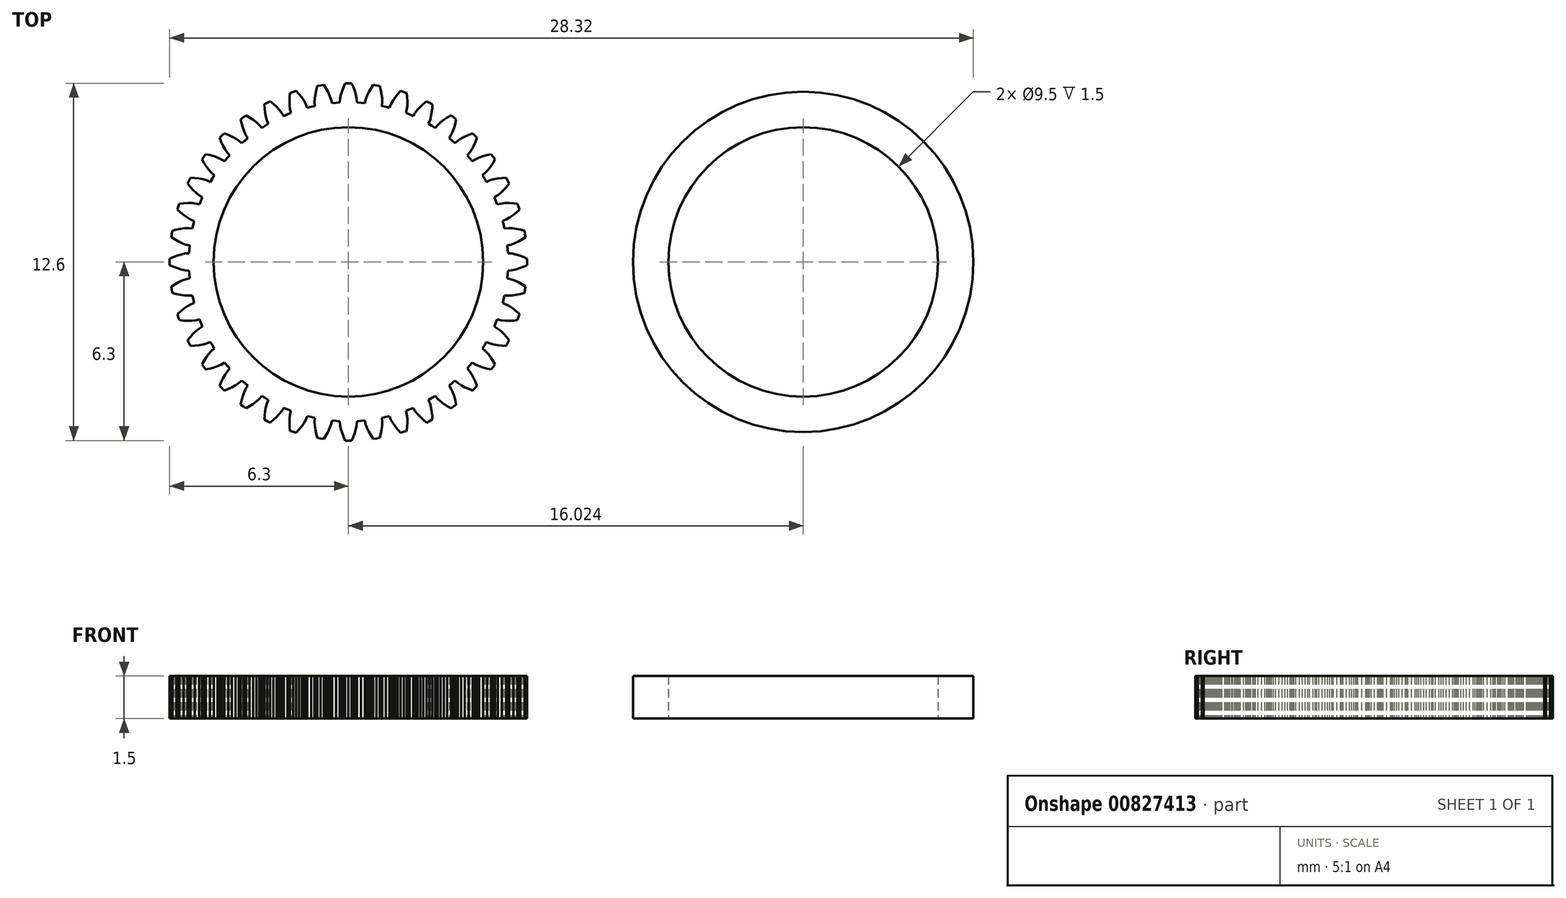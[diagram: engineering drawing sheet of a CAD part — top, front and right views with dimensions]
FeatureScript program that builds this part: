
annotation { "Feature Type Name" : "Feature", "Feature Type Description" : "" }
export const myFeature = defineFeature(function(context is Context, id is Id, definition is map)
    precondition{}
    {
        {
            var Q0;
            Q0=qCreatedBy(makeId("Top.planeOp"),FACE);
            var sketch = newSketch(context, id + "F0", { "sketchPlane" : qUnion([Q0])});
            skLineSegment(sketch, "E0", {"start": v(5.6, -0.44) * mm, "end": v(5.62, -0.3) * mm});
            skLineSegment(sketch, "E1", {"start": v(5.62, -0.3) * mm, "end": v(5.75, -0.3) * mm});
            skLineSegment(sketch, "E2", {"start": v(5.75, -0.3) * mm, "end": v(5.89, -0.27) * mm});
            skLineSegment(sketch, "E3", {"start": v(5.89, -0.27) * mm, "end": v(6.03, -0.23) * mm});
            skLineSegment(sketch, "E4", {"start": v(6.03, -0.23) * mm, "end": v(6.16, -0.17) * mm});
            skLineSegment(sketch, "E5", {"start": v(6.16, -0.17) * mm, "end": v(6.3, -0.11) * mm});
            skLineSegment(sketch, "E6", {"start": v(6.3, -0.11) * mm, "end": v(6.3, 0) * mm});
            skLineSegment(sketch, "E7", {"start": v(6.3, 0) * mm, "end": v(6.3, 0.11) * mm});
            skLineSegment(sketch, "E8", {"start": v(6.3, 0.11) * mm, "end": v(6.16, 0.17) * mm});
            skLineSegment(sketch, "E9", {"start": v(6.16, 0.17) * mm, "end": v(6.03, 0.23) * mm});
            skLineSegment(sketch, "E10", {"start": v(6.03, 0.23) * mm, "end": v(5.89, 0.27) * mm});
            skLineSegment(sketch, "E11", {"start": v(5.89, 0.27) * mm, "end": v(5.75, 0.3) * mm});
            skLineSegment(sketch, "E12", {"start": v(5.75, 0.3) * mm, "end": v(5.62, 0.3) * mm});
            skLineSegment(sketch, "E13", {"start": v(5.62, 0.3) * mm, "end": v(5.6, 0.44) * mm});
            skLineSegment(sketch, "E14", {"start": v(5.6, 0.44) * mm, "end": v(5.6, 0.58) * mm});
            skLineSegment(sketch, "E15", {"start": v(5.6, 0.58) * mm, "end": v(5.73, 0.6) * mm});
            skLineSegment(sketch, "E16", {"start": v(5.73, 0.6) * mm, "end": v(5.86, 0.66) * mm});
            skLineSegment(sketch, "E17", {"start": v(5.86, 0.66) * mm, "end": v(5.99, 0.72) * mm});
            skLineSegment(sketch, "E18", {"start": v(5.99, 0.72) * mm, "end": v(6.11, 0.8) * mm});
            skLineSegment(sketch, "E19", {"start": v(6.11, 0.8) * mm, "end": v(6.24, 0.87) * mm});
            skLineSegment(sketch, "E20", {"start": v(6.24, 0.87) * mm, "end": v(6.22, 0.99) * mm});
            skLineSegment(sketch, "E21", {"start": v(6.22, 0.99) * mm, "end": v(6.2, 1.1) * mm});
            skLineSegment(sketch, "E22", {"start": v(6.2, 1.1) * mm, "end": v(6.06, 1.14) * mm});
            skLineSegment(sketch, "E23", {"start": v(6.06, 1.14) * mm, "end": v(5.92, 1.17) * mm});
            skLineSegment(sketch, "E24", {"start": v(5.92, 1.17) * mm, "end": v(5.77, 1.18) * mm});
            skLineSegment(sketch, "E25", {"start": v(5.77, 1.18) * mm, "end": v(5.64, 1.2) * mm});
            skLineSegment(sketch, "E26", {"start": v(5.64, 1.2) * mm, "end": v(5.5, 1.18) * mm});
            skLineSegment(sketch, "E27", {"start": v(5.5, 1.18) * mm, "end": v(5.47, 1.31) * mm});
            skLineSegment(sketch, "E28", {"start": v(5.47, 1.31) * mm, "end": v(5.44, 1.45) * mm});
            skLineSegment(sketch, "E29", {"start": v(5.44, 1.45) * mm, "end": v(5.56, 1.5) * mm});
            skLineSegment(sketch, "E30", {"start": v(5.56, 1.5) * mm, "end": v(5.68, 1.57) * mm});
            skLineSegment(sketch, "E31", {"start": v(5.68, 1.57) * mm, "end": v(5.8, 1.65) * mm});
            skLineSegment(sketch, "E32", {"start": v(5.8, 1.65) * mm, "end": v(5.91, 1.74) * mm});
            skLineSegment(sketch, "E33", {"start": v(5.91, 1.74) * mm, "end": v(6.03, 1.84) * mm});
            skLineSegment(sketch, "E34", {"start": v(6.03, 1.84) * mm, "end": v(6, 1.95) * mm});
            skLineSegment(sketch, "E35", {"start": v(6, 1.95) * mm, "end": v(5.96, 2.05) * mm});
            skLineSegment(sketch, "E36", {"start": v(5.96, 2.05) * mm, "end": v(5.8, 2.07) * mm});
            skLineSegment(sketch, "E37", {"start": v(5.8, 2.07) * mm, "end": v(5.66, 2.08) * mm});
            skLineSegment(sketch, "E38", {"start": v(5.66, 2.08) * mm, "end": v(5.52, 2.07) * mm});
            skLineSegment(sketch, "E39", {"start": v(5.52, 2.07) * mm, "end": v(5.38, 2.06) * mm});
            skLineSegment(sketch, "E40", {"start": v(5.38, 2.06) * mm, "end": v(5.25, 2.03) * mm});
            skLineSegment(sketch, "E41", {"start": v(5.25, 2.03) * mm, "end": v(5.2, 2.15) * mm});
            skLineSegment(sketch, "E42", {"start": v(5.2, 2.15) * mm, "end": v(5.14, 2.28) * mm});
            skLineSegment(sketch, "E43", {"start": v(5.14, 2.28) * mm, "end": v(5.26, 2.35) * mm});
            skLineSegment(sketch, "E44", {"start": v(5.26, 2.35) * mm, "end": v(5.37, 2.44) * mm});
            skLineSegment(sketch, "E45", {"start": v(5.37, 2.44) * mm, "end": v(5.47, 2.53) * mm});
            skLineSegment(sketch, "E46", {"start": v(5.47, 2.53) * mm, "end": v(5.57, 2.64) * mm});
            skLineSegment(sketch, "E47", {"start": v(5.57, 2.64) * mm, "end": v(5.66, 2.76) * mm});
            skLineSegment(sketch, "E48", {"start": v(5.66, 2.76) * mm, "end": v(5.61, 2.86) * mm});
            skLineSegment(sketch, "E49", {"start": v(5.61, 2.86) * mm, "end": v(5.56, 2.96) * mm});
            skLineSegment(sketch, "E50", {"start": v(5.56, 2.96) * mm, "end": v(5.41, 2.95) * mm});
            skLineSegment(sketch, "E51", {"start": v(5.41, 2.95) * mm, "end": v(5.27, 2.94) * mm});
            skLineSegment(sketch, "E52", {"start": v(5.27, 2.94) * mm, "end": v(5.13, 2.91) * mm});
            skLineSegment(sketch, "E53", {"start": v(5.13, 2.91) * mm, "end": v(5, 2.87) * mm});
            skLineSegment(sketch, "E54", {"start": v(5, 2.87) * mm, "end": v(4.87, 2.82) * mm});
            skLineSegment(sketch, "E55", {"start": v(4.87, 2.82) * mm, "end": v(4.8, 2.94) * mm});
            skLineSegment(sketch, "E56", {"start": v(4.8, 2.94) * mm, "end": v(4.72, 3.06) * mm});
            skLineSegment(sketch, "E57", {"start": v(4.72, 3.06) * mm, "end": v(4.83, 3.14) * mm});
            skLineSegment(sketch, "E58", {"start": v(4.83, 3.14) * mm, "end": v(4.92, 3.25) * mm});
            skLineSegment(sketch, "E59", {"start": v(4.92, 3.25) * mm, "end": v(5, 3.36) * mm});
            skLineSegment(sketch, "E60", {"start": v(5, 3.36) * mm, "end": v(5.09, 3.48) * mm});
            skLineSegment(sketch, "E61", {"start": v(5.09, 3.48) * mm, "end": v(5.16, 3.61) * mm});
            skLineSegment(sketch, "E62", {"start": v(5.16, 3.61) * mm, "end": v(5.1, 3.7) * mm});
            skLineSegment(sketch, "E63", {"start": v(5.1, 3.7) * mm, "end": v(5.03, 3.8) * mm});
            skLineSegment(sketch, "E64", {"start": v(5.03, 3.8) * mm, "end": v(4.88, 3.76) * mm});
            skLineSegment(sketch, "E65", {"start": v(4.88, 3.76) * mm, "end": v(4.74, 3.72) * mm});
            skLineSegment(sketch, "E66", {"start": v(4.74, 3.72) * mm, "end": v(4.6, 3.68) * mm});
            skLineSegment(sketch, "E67", {"start": v(4.6, 3.68) * mm, "end": v(4.48, 3.62) * mm});
            skLineSegment(sketch, "E68", {"start": v(4.48, 3.62) * mm, "end": v(4.37, 3.55) * mm});
            skLineSegment(sketch, "E69", {"start": v(4.37, 3.55) * mm, "end": v(4.28, 3.65) * mm});
            skLineSegment(sketch, "E70", {"start": v(4.28, 3.65) * mm, "end": v(4.19, 3.76) * mm});
            skLineSegment(sketch, "E71", {"start": v(4.19, 3.76) * mm, "end": v(4.28, 3.86) * mm});
            skLineSegment(sketch, "E72", {"start": v(4.28, 3.86) * mm, "end": v(4.35, 3.98) * mm});
            skLineSegment(sketch, "E73", {"start": v(4.35, 3.98) * mm, "end": v(4.42, 4.1) * mm});
            skLineSegment(sketch, "E74", {"start": v(4.42, 4.1) * mm, "end": v(4.48, 4.23) * mm});
            skLineSegment(sketch, "E75", {"start": v(4.48, 4.23) * mm, "end": v(4.53, 4.37) * mm});
            skLineSegment(sketch, "E76", {"start": v(4.53, 4.37) * mm, "end": v(4.45, 4.45) * mm});
            skLineSegment(sketch, "E77", {"start": v(4.45, 4.45) * mm, "end": v(4.37, 4.53) * mm});
            skLineSegment(sketch, "E78", {"start": v(4.37, 4.53) * mm, "end": v(4.23, 4.48) * mm});
            skLineSegment(sketch, "E79", {"start": v(4.23, 4.48) * mm, "end": v(4.1, 4.42) * mm});
            skLineSegment(sketch, "E80", {"start": v(4.1, 4.42) * mm, "end": v(3.98, 4.35) * mm});
            skLineSegment(sketch, "E81", {"start": v(3.98, 4.35) * mm, "end": v(3.86, 4.28) * mm});
            skLineSegment(sketch, "E82", {"start": v(3.86, 4.28) * mm, "end": v(3.76, 4.19) * mm});
            skLineSegment(sketch, "E83", {"start": v(3.76, 4.19) * mm, "end": v(3.65, 4.28) * mm});
            skLineSegment(sketch, "E84", {"start": v(3.65, 4.28) * mm, "end": v(3.55, 4.37) * mm});
            skLineSegment(sketch, "E85", {"start": v(3.55, 4.37) * mm, "end": v(3.62, 4.48) * mm});
            skLineSegment(sketch, "E86", {"start": v(3.62, 4.48) * mm, "end": v(3.68, 4.6) * mm});
            skLineSegment(sketch, "E87", {"start": v(3.68, 4.6) * mm, "end": v(3.72, 4.74) * mm});
            skLineSegment(sketch, "E88", {"start": v(3.72, 4.74) * mm, "end": v(3.76, 4.88) * mm});
            skLineSegment(sketch, "E89", {"start": v(3.76, 4.88) * mm, "end": v(3.8, 5.03) * mm});
            skLineSegment(sketch, "E90", {"start": v(3.8, 5.03) * mm, "end": v(3.7, 5.1) * mm});
            skLineSegment(sketch, "E91", {"start": v(3.7, 5.1) * mm, "end": v(3.61, 5.16) * mm});
            skLineSegment(sketch, "E92", {"start": v(3.61, 5.16) * mm, "end": v(3.48, 5.09) * mm});
            skLineSegment(sketch, "E93", {"start": v(3.48, 5.09) * mm, "end": v(3.36, 5) * mm});
            skLineSegment(sketch, "E94", {"start": v(3.36, 5) * mm, "end": v(3.25, 4.92) * mm});
            skLineSegment(sketch, "E95", {"start": v(3.25, 4.92) * mm, "end": v(3.14, 4.83) * mm});
            skLineSegment(sketch, "E96", {"start": v(3.14, 4.83) * mm, "end": v(3.06, 4.72) * mm});
            skLineSegment(sketch, "E97", {"start": v(3.06, 4.72) * mm, "end": v(2.94, 4.8) * mm});
            skLineSegment(sketch, "E98", {"start": v(2.94, 4.8) * mm, "end": v(2.82, 4.87) * mm});
            skLineSegment(sketch, "E99", {"start": v(2.82, 4.87) * mm, "end": v(2.87, 5) * mm});
            skLineSegment(sketch, "E100", {"start": v(2.87, 5) * mm, "end": v(2.91, 5.13) * mm});
            skLineSegment(sketch, "E101", {"start": v(2.91, 5.13) * mm, "end": v(2.94, 5.27) * mm});
            skLineSegment(sketch, "E102", {"start": v(2.94, 5.27) * mm, "end": v(2.95, 5.41) * mm});
            skLineSegment(sketch, "E103", {"start": v(2.95, 5.41) * mm, "end": v(2.96, 5.56) * mm});
            skLineSegment(sketch, "E104", {"start": v(2.96, 5.56) * mm, "end": v(2.86, 5.61) * mm});
            skLineSegment(sketch, "E105", {"start": v(2.86, 5.61) * mm, "end": v(2.76, 5.66) * mm});
            skLineSegment(sketch, "E106", {"start": v(2.76, 5.66) * mm, "end": v(2.64, 5.57) * mm});
            skLineSegment(sketch, "E107", {"start": v(2.64, 5.57) * mm, "end": v(2.53, 5.47) * mm});
            skLineSegment(sketch, "E108", {"start": v(2.53, 5.47) * mm, "end": v(2.44, 5.37) * mm});
            skLineSegment(sketch, "E109", {"start": v(2.44, 5.37) * mm, "end": v(2.35, 5.26) * mm});
            skLineSegment(sketch, "E110", {"start": v(2.35, 5.26) * mm, "end": v(2.28, 5.14) * mm});
            skLineSegment(sketch, "E111", {"start": v(2.28, 5.14) * mm, "end": v(2.15, 5.2) * mm});
            skLineSegment(sketch, "E112", {"start": v(2.15, 5.2) * mm, "end": v(2.03, 5.25) * mm});
            skLineSegment(sketch, "E113", {"start": v(2.03, 5.25) * mm, "end": v(2.06, 5.38) * mm});
            skLineSegment(sketch, "E114", {"start": v(2.06, 5.38) * mm, "end": v(2.07, 5.52) * mm});
            skLineSegment(sketch, "E115", {"start": v(2.07, 5.52) * mm, "end": v(2.08, 5.66) * mm});
            skLineSegment(sketch, "E116", {"start": v(2.08, 5.66) * mm, "end": v(2.07, 5.8) * mm});
            skLineSegment(sketch, "E117", {"start": v(2.07, 5.8) * mm, "end": v(2.05, 5.96) * mm});
            skLineSegment(sketch, "E118", {"start": v(2.05, 5.96) * mm, "end": v(1.95, 6) * mm});
            skLineSegment(sketch, "E119", {"start": v(1.95, 6) * mm, "end": v(1.84, 6.03) * mm});
            skLineSegment(sketch, "E120", {"start": v(1.84, 6.03) * mm, "end": v(1.74, 5.91) * mm});
            skLineSegment(sketch, "E121", {"start": v(1.74, 5.91) * mm, "end": v(1.65, 5.8) * mm});
            skLineSegment(sketch, "E122", {"start": v(1.65, 5.8) * mm, "end": v(1.57, 5.68) * mm});
            skLineSegment(sketch, "E123", {"start": v(1.57, 5.68) * mm, "end": v(1.5, 5.56) * mm});
            skLineSegment(sketch, "E124", {"start": v(1.5, 5.56) * mm, "end": v(1.45, 5.44) * mm});
            skLineSegment(sketch, "E125", {"start": v(1.45, 5.44) * mm, "end": v(1.31, 5.47) * mm});
            skLineSegment(sketch, "E126", {"start": v(1.31, 5.47) * mm, "end": v(1.18, 5.5) * mm});
            skLineSegment(sketch, "E127", {"start": v(1.18, 5.5) * mm, "end": v(1.2, 5.64) * mm});
            skLineSegment(sketch, "E128", {"start": v(1.2, 5.64) * mm, "end": v(1.18, 5.77) * mm});
            skLineSegment(sketch, "E129", {"start": v(1.18, 5.77) * mm, "end": v(1.17, 5.92) * mm});
            skLineSegment(sketch, "E130", {"start": v(1.17, 5.92) * mm, "end": v(1.14, 6.06) * mm});
            skLineSegment(sketch, "E131", {"start": v(1.14, 6.06) * mm, "end": v(1.1, 6.2) * mm});
            skLineSegment(sketch, "E132", {"start": v(1.1, 6.2) * mm, "end": v(0.99, 6.22) * mm});
            skLineSegment(sketch, "E133", {"start": v(0.99, 6.22) * mm, "end": v(0.87, 6.24) * mm});
            skLineSegment(sketch, "E134", {"start": v(0.87, 6.24) * mm, "end": v(0.8, 6.11) * mm});
            skLineSegment(sketch, "E135", {"start": v(0.8, 6.11) * mm, "end": v(0.72, 5.99) * mm});
            skLineSegment(sketch, "E136", {"start": v(0.72, 5.99) * mm, "end": v(0.66, 5.86) * mm});
            skLineSegment(sketch, "E137", {"start": v(0.66, 5.86) * mm, "end": v(0.6, 5.73) * mm});
            skLineSegment(sketch, "E138", {"start": v(0.6, 5.73) * mm, "end": v(0.58, 5.6) * mm});
            skLineSegment(sketch, "E139", {"start": v(0.58, 5.6) * mm, "end": v(0.44, 5.6) * mm});
            skLineSegment(sketch, "E140", {"start": v(0.44, 5.6) * mm, "end": v(0.3, 5.62) * mm});
            skLineSegment(sketch, "E141", {"start": v(0.3, 5.62) * mm, "end": v(0.3, 5.75) * mm});
            skLineSegment(sketch, "E142", {"start": v(0.3, 5.75) * mm, "end": v(0.27, 5.89) * mm});
            skLineSegment(sketch, "E143", {"start": v(0.27, 5.89) * mm, "end": v(0.23, 6.03) * mm});
            skLineSegment(sketch, "E144", {"start": v(0.23, 6.03) * mm, "end": v(0.17, 6.16) * mm});
            skLineSegment(sketch, "E145", {"start": v(0.17, 6.16) * mm, "end": v(0.11, 6.3) * mm});
            skLineSegment(sketch, "E146", {"start": v(0.11, 6.3) * mm, "end": v(0, 6.3) * mm});
            skLineSegment(sketch, "E147", {"start": v(0, 6.3) * mm, "end": v(-0.11, 6.3) * mm});
            skLineSegment(sketch, "E148", {"start": v(-0.11, 6.3) * mm, "end": v(-0.17, 6.16) * mm});
            skLineSegment(sketch, "E149", {"start": v(-0.17, 6.16) * mm, "end": v(-0.23, 6.03) * mm});
            skLineSegment(sketch, "E150", {"start": v(-0.23, 6.03) * mm, "end": v(-0.27, 5.89) * mm});
            skLineSegment(sketch, "E151", {"start": v(-0.27, 5.89) * mm, "end": v(-0.3, 5.75) * mm});
            skLineSegment(sketch, "E152", {"start": v(-0.3, 5.75) * mm, "end": v(-0.3, 5.62) * mm});
            skLineSegment(sketch, "E153", {"start": v(-0.3, 5.62) * mm, "end": v(-0.44, 5.6) * mm});
            skLineSegment(sketch, "E154", {"start": v(-0.44, 5.6) * mm, "end": v(-0.58, 5.6) * mm});
            skLineSegment(sketch, "E155", {"start": v(-0.58, 5.6) * mm, "end": v(-0.6, 5.73) * mm});
            skLineSegment(sketch, "E156", {"start": v(-0.6, 5.73) * mm, "end": v(-0.66, 5.86) * mm});
            skLineSegment(sketch, "E157", {"start": v(-0.66, 5.86) * mm, "end": v(-0.72, 5.99) * mm});
            skLineSegment(sketch, "E158", {"start": v(-0.72, 5.99) * mm, "end": v(-0.8, 6.11) * mm});
            skLineSegment(sketch, "E159", {"start": v(-0.8, 6.11) * mm, "end": v(-0.87, 6.24) * mm});
            skLineSegment(sketch, "E160", {"start": v(-0.87, 6.24) * mm, "end": v(-0.99, 6.22) * mm});
            skLineSegment(sketch, "E161", {"start": v(-0.99, 6.22) * mm, "end": v(-1.1, 6.2) * mm});
            skLineSegment(sketch, "E162", {"start": v(-1.1, 6.2) * mm, "end": v(-1.14, 6.06) * mm});
            skLineSegment(sketch, "E163", {"start": v(-1.14, 6.06) * mm, "end": v(-1.17, 5.92) * mm});
            skLineSegment(sketch, "E164", {"start": v(-1.17, 5.92) * mm, "end": v(-1.18, 5.77) * mm});
            skLineSegment(sketch, "E165", {"start": v(-1.18, 5.77) * mm, "end": v(-1.2, 5.64) * mm});
            skLineSegment(sketch, "E166", {"start": v(-1.2, 5.64) * mm, "end": v(-1.18, 5.5) * mm});
            skLineSegment(sketch, "E167", {"start": v(-1.18, 5.5) * mm, "end": v(-1.31, 5.47) * mm});
            skLineSegment(sketch, "E168", {"start": v(-1.31, 5.47) * mm, "end": v(-1.45, 5.44) * mm});
            skLineSegment(sketch, "E169", {"start": v(-1.45, 5.44) * mm, "end": v(-1.5, 5.56) * mm});
            skLineSegment(sketch, "E170", {"start": v(-1.5, 5.56) * mm, "end": v(-1.57, 5.68) * mm});
            skLineSegment(sketch, "E171", {"start": v(-1.57, 5.68) * mm, "end": v(-1.65, 5.8) * mm});
            skLineSegment(sketch, "E172", {"start": v(-1.65, 5.8) * mm, "end": v(-1.74, 5.91) * mm});
            skLineSegment(sketch, "E173", {"start": v(-1.74, 5.91) * mm, "end": v(-1.84, 6.03) * mm});
            skLineSegment(sketch, "E174", {"start": v(-1.84, 6.03) * mm, "end": v(-1.95, 6) * mm});
            skLineSegment(sketch, "E175", {"start": v(-1.95, 6) * mm, "end": v(-2.05, 5.96) * mm});
            skLineSegment(sketch, "E176", {"start": v(-2.05, 5.96) * mm, "end": v(-2.07, 5.8) * mm});
            skLineSegment(sketch, "E177", {"start": v(-2.07, 5.8) * mm, "end": v(-2.08, 5.66) * mm});
            skLineSegment(sketch, "E178", {"start": v(-2.08, 5.66) * mm, "end": v(-2.07, 5.52) * mm});
            skLineSegment(sketch, "E179", {"start": v(-2.07, 5.52) * mm, "end": v(-2.06, 5.38) * mm});
            skLineSegment(sketch, "E180", {"start": v(-2.06, 5.38) * mm, "end": v(-2.03, 5.25) * mm});
            skLineSegment(sketch, "E181", {"start": v(-2.03, 5.25) * mm, "end": v(-2.15, 5.2) * mm});
            skLineSegment(sketch, "E182", {"start": v(-2.15, 5.2) * mm, "end": v(-2.28, 5.14) * mm});
            skLineSegment(sketch, "E183", {"start": v(-2.28, 5.14) * mm, "end": v(-2.35, 5.26) * mm});
            skLineSegment(sketch, "E184", {"start": v(-2.35, 5.26) * mm, "end": v(-2.44, 5.37) * mm});
            skLineSegment(sketch, "E185", {"start": v(-2.44, 5.37) * mm, "end": v(-2.53, 5.47) * mm});
            skLineSegment(sketch, "E186", {"start": v(-2.53, 5.47) * mm, "end": v(-2.64, 5.57) * mm});
            skLineSegment(sketch, "E187", {"start": v(-2.64, 5.57) * mm, "end": v(-2.76, 5.66) * mm});
            skLineSegment(sketch, "E188", {"start": v(-2.76, 5.66) * mm, "end": v(-2.86, 5.61) * mm});
            skLineSegment(sketch, "E189", {"start": v(-2.86, 5.61) * mm, "end": v(-2.96, 5.56) * mm});
            skLineSegment(sketch, "E190", {"start": v(-2.96, 5.56) * mm, "end": v(-2.95, 5.41) * mm});
            skLineSegment(sketch, "E191", {"start": v(-2.95, 5.41) * mm, "end": v(-2.94, 5.27) * mm});
            skLineSegment(sketch, "E192", {"start": v(-2.94, 5.27) * mm, "end": v(-2.91, 5.13) * mm});
            skLineSegment(sketch, "E193", {"start": v(-2.91, 5.13) * mm, "end": v(-2.87, 5) * mm});
            skLineSegment(sketch, "E194", {"start": v(-2.87, 5) * mm, "end": v(-2.82, 4.87) * mm});
            skLineSegment(sketch, "E195", {"start": v(-2.82, 4.87) * mm, "end": v(-2.94, 4.8) * mm});
            skLineSegment(sketch, "E196", {"start": v(-2.94, 4.8) * mm, "end": v(-3.06, 4.72) * mm});
            skLineSegment(sketch, "E197", {"start": v(-3.06, 4.72) * mm, "end": v(-3.14, 4.83) * mm});
            skLineSegment(sketch, "E198", {"start": v(-3.14, 4.83) * mm, "end": v(-3.25, 4.92) * mm});
            skLineSegment(sketch, "E199", {"start": v(-3.25, 4.92) * mm, "end": v(-3.36, 5) * mm});
            skLineSegment(sketch, "E200", {"start": v(-3.36, 5) * mm, "end": v(-3.48, 5.09) * mm});
            skLineSegment(sketch, "E201", {"start": v(-3.48, 5.09) * mm, "end": v(-3.61, 5.16) * mm});
            skLineSegment(sketch, "E202", {"start": v(-3.61, 5.16) * mm, "end": v(-3.7, 5.1) * mm});
            skLineSegment(sketch, "E203", {"start": v(-3.7, 5.1) * mm, "end": v(-3.8, 5.03) * mm});
            skLineSegment(sketch, "E204", {"start": v(-3.8, 5.03) * mm, "end": v(-3.76, 4.88) * mm});
            skLineSegment(sketch, "E205", {"start": v(-3.76, 4.88) * mm, "end": v(-3.72, 4.74) * mm});
            skLineSegment(sketch, "E206", {"start": v(-3.72, 4.74) * mm, "end": v(-3.68, 4.6) * mm});
            skLineSegment(sketch, "E207", {"start": v(-3.68, 4.6) * mm, "end": v(-3.62, 4.48) * mm});
            skLineSegment(sketch, "E208", {"start": v(-3.62, 4.48) * mm, "end": v(-3.55, 4.37) * mm});
            skLineSegment(sketch, "E209", {"start": v(-3.55, 4.37) * mm, "end": v(-3.65, 4.28) * mm});
            skLineSegment(sketch, "E210", {"start": v(-3.65, 4.28) * mm, "end": v(-3.76, 4.19) * mm});
            skLineSegment(sketch, "E211", {"start": v(-3.76, 4.19) * mm, "end": v(-3.86, 4.28) * mm});
            skLineSegment(sketch, "E212", {"start": v(-3.86, 4.28) * mm, "end": v(-3.98, 4.35) * mm});
            skLineSegment(sketch, "E213", {"start": v(-3.98, 4.35) * mm, "end": v(-4.1, 4.42) * mm});
            skLineSegment(sketch, "E214", {"start": v(-4.1, 4.42) * mm, "end": v(-4.23, 4.48) * mm});
            skLineSegment(sketch, "E215", {"start": v(-4.23, 4.48) * mm, "end": v(-4.37, 4.53) * mm});
            skLineSegment(sketch, "E216", {"start": v(-4.37, 4.53) * mm, "end": v(-4.45, 4.45) * mm});
            skLineSegment(sketch, "E217", {"start": v(-4.45, 4.45) * mm, "end": v(-4.53, 4.37) * mm});
            skLineSegment(sketch, "E218", {"start": v(-4.53, 4.37) * mm, "end": v(-4.48, 4.23) * mm});
            skLineSegment(sketch, "E219", {"start": v(-4.48, 4.23) * mm, "end": v(-4.42, 4.1) * mm});
            skLineSegment(sketch, "E220", {"start": v(-4.42, 4.1) * mm, "end": v(-4.35, 3.98) * mm});
            skLineSegment(sketch, "E221", {"start": v(-4.35, 3.98) * mm, "end": v(-4.28, 3.86) * mm});
            skLineSegment(sketch, "E222", {"start": v(-4.28, 3.86) * mm, "end": v(-4.19, 3.76) * mm});
            skLineSegment(sketch, "E223", {"start": v(-4.19, 3.76) * mm, "end": v(-4.28, 3.65) * mm});
            skLineSegment(sketch, "E224", {"start": v(-4.28, 3.65) * mm, "end": v(-4.37, 3.55) * mm});
            skLineSegment(sketch, "E225", {"start": v(-4.37, 3.55) * mm, "end": v(-4.48, 3.62) * mm});
            skLineSegment(sketch, "E226", {"start": v(-4.48, 3.62) * mm, "end": v(-4.6, 3.68) * mm});
            skLineSegment(sketch, "E227", {"start": v(-4.6, 3.68) * mm, "end": v(-4.74, 3.72) * mm});
            skLineSegment(sketch, "E228", {"start": v(-4.74, 3.72) * mm, "end": v(-4.88, 3.76) * mm});
            skLineSegment(sketch, "E229", {"start": v(-4.88, 3.76) * mm, "end": v(-5.03, 3.8) * mm});
            skLineSegment(sketch, "E230", {"start": v(-5.03, 3.8) * mm, "end": v(-5.1, 3.7) * mm});
            skLineSegment(sketch, "E231", {"start": v(-5.1, 3.7) * mm, "end": v(-5.16, 3.61) * mm});
            skLineSegment(sketch, "E232", {"start": v(-5.16, 3.61) * mm, "end": v(-5.09, 3.48) * mm});
            skLineSegment(sketch, "E233", {"start": v(-5.09, 3.48) * mm, "end": v(-5, 3.36) * mm});
            skLineSegment(sketch, "E234", {"start": v(-5, 3.36) * mm, "end": v(-4.92, 3.25) * mm});
            skLineSegment(sketch, "E235", {"start": v(-4.92, 3.25) * mm, "end": v(-4.83, 3.14) * mm});
            skLineSegment(sketch, "E236", {"start": v(-4.83, 3.14) * mm, "end": v(-4.72, 3.06) * mm});
            skLineSegment(sketch, "E237", {"start": v(-4.72, 3.06) * mm, "end": v(-4.8, 2.94) * mm});
            skLineSegment(sketch, "E238", {"start": v(-4.8, 2.94) * mm, "end": v(-4.87, 2.82) * mm});
            skLineSegment(sketch, "E239", {"start": v(-4.87, 2.82) * mm, "end": v(-5, 2.87) * mm});
            skLineSegment(sketch, "E240", {"start": v(-5, 2.87) * mm, "end": v(-5.13, 2.91) * mm});
            skLineSegment(sketch, "E241", {"start": v(-5.13, 2.91) * mm, "end": v(-5.27, 2.94) * mm});
            skLineSegment(sketch, "E242", {"start": v(-5.27, 2.94) * mm, "end": v(-5.41, 2.95) * mm});
            skLineSegment(sketch, "E243", {"start": v(-5.41, 2.95) * mm, "end": v(-5.56, 2.96) * mm});
            skLineSegment(sketch, "E244", {"start": v(-5.56, 2.96) * mm, "end": v(-5.61, 2.86) * mm});
            skLineSegment(sketch, "E245", {"start": v(-5.61, 2.86) * mm, "end": v(-5.66, 2.76) * mm});
            skLineSegment(sketch, "E246", {"start": v(-5.66, 2.76) * mm, "end": v(-5.57, 2.64) * mm});
            skLineSegment(sketch, "E247", {"start": v(-5.57, 2.64) * mm, "end": v(-5.47, 2.53) * mm});
            skLineSegment(sketch, "E248", {"start": v(-5.47, 2.53) * mm, "end": v(-5.37, 2.44) * mm});
            skLineSegment(sketch, "E249", {"start": v(-5.37, 2.44) * mm, "end": v(-5.26, 2.35) * mm});
            skLineSegment(sketch, "E250", {"start": v(-5.26, 2.35) * mm, "end": v(-5.14, 2.28) * mm});
            skLineSegment(sketch, "E251", {"start": v(-5.14, 2.28) * mm, "end": v(-5.2, 2.15) * mm});
            skLineSegment(sketch, "E252", {"start": v(-5.2, 2.15) * mm, "end": v(-5.25, 2.03) * mm});
            skLineSegment(sketch, "E253", {"start": v(-5.25, 2.03) * mm, "end": v(-5.38, 2.06) * mm});
            skLineSegment(sketch, "E254", {"start": v(-5.38, 2.06) * mm, "end": v(-5.52, 2.07) * mm});
            skLineSegment(sketch, "E255", {"start": v(-5.52, 2.07) * mm, "end": v(-5.66, 2.08) * mm});
            skLineSegment(sketch, "E256", {"start": v(-5.66, 2.08) * mm, "end": v(-5.8, 2.07) * mm});
            skLineSegment(sketch, "E257", {"start": v(-5.8, 2.07) * mm, "end": v(-5.96, 2.05) * mm});
            skLineSegment(sketch, "E258", {"start": v(-5.96, 2.05) * mm, "end": v(-6, 1.95) * mm});
            skLineSegment(sketch, "E259", {"start": v(-6, 1.95) * mm, "end": v(-6.03, 1.84) * mm});
            skLineSegment(sketch, "E260", {"start": v(-6.03, 1.84) * mm, "end": v(-5.91, 1.74) * mm});
            skLineSegment(sketch, "E261", {"start": v(-5.91, 1.74) * mm, "end": v(-5.8, 1.65) * mm});
            skLineSegment(sketch, "E262", {"start": v(-5.8, 1.65) * mm, "end": v(-5.68, 1.57) * mm});
            skLineSegment(sketch, "E263", {"start": v(-5.68, 1.57) * mm, "end": v(-5.56, 1.5) * mm});
            skLineSegment(sketch, "E264", {"start": v(-5.56, 1.5) * mm, "end": v(-5.44, 1.45) * mm});
            skLineSegment(sketch, "E265", {"start": v(-5.44, 1.45) * mm, "end": v(-5.47, 1.31) * mm});
            skLineSegment(sketch, "E266", {"start": v(-5.47, 1.31) * mm, "end": v(-5.5, 1.18) * mm});
            skLineSegment(sketch, "E267", {"start": v(-5.5, 1.18) * mm, "end": v(-5.64, 1.2) * mm});
            skLineSegment(sketch, "E268", {"start": v(-5.64, 1.2) * mm, "end": v(-5.77, 1.18) * mm});
            skLineSegment(sketch, "E269", {"start": v(-5.77, 1.18) * mm, "end": v(-5.92, 1.17) * mm});
            skLineSegment(sketch, "E270", {"start": v(-5.92, 1.17) * mm, "end": v(-6.06, 1.14) * mm});
            skLineSegment(sketch, "E271", {"start": v(-6.06, 1.14) * mm, "end": v(-6.2, 1.1) * mm});
            skLineSegment(sketch, "E272", {"start": v(-6.2, 1.1) * mm, "end": v(-6.22, 0.99) * mm});
            skLineSegment(sketch, "E273", {"start": v(-6.22, 0.99) * mm, "end": v(-6.24, 0.87) * mm});
            skLineSegment(sketch, "E274", {"start": v(-6.24, 0.87) * mm, "end": v(-6.11, 0.8) * mm});
            skLineSegment(sketch, "E275", {"start": v(-6.11, 0.8) * mm, "end": v(-5.99, 0.72) * mm});
            skLineSegment(sketch, "E276", {"start": v(-5.99, 0.72) * mm, "end": v(-5.86, 0.66) * mm});
            skLineSegment(sketch, "E277", {"start": v(-5.86, 0.66) * mm, "end": v(-5.73, 0.6) * mm});
            skLineSegment(sketch, "E278", {"start": v(-5.73, 0.6) * mm, "end": v(-5.6, 0.58) * mm});
            skLineSegment(sketch, "E279", {"start": v(-5.6, 0.58) * mm, "end": v(-5.6, 0.44) * mm});
            skLineSegment(sketch, "E280", {"start": v(-5.6, 0.44) * mm, "end": v(-5.62, 0.3) * mm});
            skLineSegment(sketch, "E281", {"start": v(-5.62, 0.3) * mm, "end": v(-5.75, 0.3) * mm});
            skLineSegment(sketch, "E282", {"start": v(-5.75, 0.3) * mm, "end": v(-5.89, 0.27) * mm});
            skLineSegment(sketch, "E283", {"start": v(-5.89, 0.27) * mm, "end": v(-6.03, 0.23) * mm});
            skLineSegment(sketch, "E284", {"start": v(-6.03, 0.23) * mm, "end": v(-6.16, 0.17) * mm});
            skLineSegment(sketch, "E285", {"start": v(-6.16, 0.17) * mm, "end": v(-6.3, 0.11) * mm});
            skLineSegment(sketch, "E286", {"start": v(-6.3, 0.11) * mm, "end": v(-6.3, 0) * mm});
            skLineSegment(sketch, "E287", {"start": v(-6.3, 0) * mm, "end": v(-6.3, -0.11) * mm});
            skLineSegment(sketch, "E288", {"start": v(-6.3, -0.11) * mm, "end": v(-6.16, -0.17) * mm});
            skLineSegment(sketch, "E289", {"start": v(-6.16, -0.17) * mm, "end": v(-6.03, -0.23) * mm});
            skLineSegment(sketch, "E290", {"start": v(-6.03, -0.23) * mm, "end": v(-5.89, -0.27) * mm});
            skLineSegment(sketch, "E291", {"start": v(-5.89, -0.27) * mm, "end": v(-5.75, -0.3) * mm});
            skLineSegment(sketch, "E292", {"start": v(-5.75, -0.3) * mm, "end": v(-5.62, -0.3) * mm});
            skLineSegment(sketch, "E293", {"start": v(-5.62, -0.3) * mm, "end": v(-5.6, -0.44) * mm});
            skLineSegment(sketch, "E294", {"start": v(-5.6, -0.44) * mm, "end": v(-5.6, -0.58) * mm});
            skLineSegment(sketch, "E295", {"start": v(-5.6, -0.58) * mm, "end": v(-5.73, -0.6) * mm});
            skLineSegment(sketch, "E296", {"start": v(-5.73, -0.6) * mm, "end": v(-5.86, -0.66) * mm});
            skLineSegment(sketch, "E297", {"start": v(-5.86, -0.66) * mm, "end": v(-5.99, -0.72) * mm});
            skLineSegment(sketch, "E298", {"start": v(-5.99, -0.72) * mm, "end": v(-6.11, -0.8) * mm});
            skLineSegment(sketch, "E299", {"start": v(-6.11, -0.8) * mm, "end": v(-6.24, -0.87) * mm});
            skLineSegment(sketch, "E300", {"start": v(-6.24, -0.87) * mm, "end": v(-6.22, -0.99) * mm});
            skLineSegment(sketch, "E301", {"start": v(-6.22, -0.99) * mm, "end": v(-6.2, -1.1) * mm});
            skLineSegment(sketch, "E302", {"start": v(-6.2, -1.1) * mm, "end": v(-6.06, -1.14) * mm});
            skLineSegment(sketch, "E303", {"start": v(-6.06, -1.14) * mm, "end": v(-5.92, -1.17) * mm});
            skLineSegment(sketch, "E304", {"start": v(-5.92, -1.17) * mm, "end": v(-5.77, -1.18) * mm});
            skLineSegment(sketch, "E305", {"start": v(-5.77, -1.18) * mm, "end": v(-5.64, -1.2) * mm});
            skLineSegment(sketch, "E306", {"start": v(-5.64, -1.2) * mm, "end": v(-5.5, -1.18) * mm});
            skLineSegment(sketch, "E307", {"start": v(-5.5, -1.18) * mm, "end": v(-5.47, -1.31) * mm});
            skLineSegment(sketch, "E308", {"start": v(-5.47, -1.31) * mm, "end": v(-5.44, -1.45) * mm});
            skLineSegment(sketch, "E309", {"start": v(-5.44, -1.45) * mm, "end": v(-5.56, -1.5) * mm});
            skLineSegment(sketch, "E310", {"start": v(-5.56, -1.5) * mm, "end": v(-5.68, -1.57) * mm});
            skLineSegment(sketch, "E311", {"start": v(-5.68, -1.57) * mm, "end": v(-5.8, -1.65) * mm});
            skLineSegment(sketch, "E312", {"start": v(-5.8, -1.65) * mm, "end": v(-5.91, -1.74) * mm});
            skLineSegment(sketch, "E313", {"start": v(-5.91, -1.74) * mm, "end": v(-6.03, -1.84) * mm});
            skLineSegment(sketch, "E314", {"start": v(-6.03, -1.84) * mm, "end": v(-6, -1.95) * mm});
            skLineSegment(sketch, "E315", {"start": v(-6, -1.95) * mm, "end": v(-5.96, -2.05) * mm});
            skLineSegment(sketch, "E316", {"start": v(-5.96, -2.05) * mm, "end": v(-5.8, -2.07) * mm});
            skLineSegment(sketch, "E317", {"start": v(-5.8, -2.07) * mm, "end": v(-5.66, -2.08) * mm});
            skLineSegment(sketch, "E318", {"start": v(-5.66, -2.08) * mm, "end": v(-5.52, -2.07) * mm});
            skLineSegment(sketch, "E319", {"start": v(-5.52, -2.07) * mm, "end": v(-5.38, -2.06) * mm});
            skLineSegment(sketch, "E320", {"start": v(-5.38, -2.06) * mm, "end": v(-5.25, -2.03) * mm});
            skLineSegment(sketch, "E321", {"start": v(-5.25, -2.03) * mm, "end": v(-5.2, -2.15) * mm});
            skLineSegment(sketch, "E322", {"start": v(-5.2, -2.15) * mm, "end": v(-5.14, -2.28) * mm});
            skLineSegment(sketch, "E323", {"start": v(-5.14, -2.28) * mm, "end": v(-5.26, -2.35) * mm});
            skLineSegment(sketch, "E324", {"start": v(-5.26, -2.35) * mm, "end": v(-5.37, -2.44) * mm});
            skLineSegment(sketch, "E325", {"start": v(-5.37, -2.44) * mm, "end": v(-5.47, -2.53) * mm});
            skLineSegment(sketch, "E326", {"start": v(-5.47, -2.53) * mm, "end": v(-5.57, -2.64) * mm});
            skLineSegment(sketch, "E327", {"start": v(-5.57, -2.64) * mm, "end": v(-5.66, -2.76) * mm});
            skLineSegment(sketch, "E328", {"start": v(-5.66, -2.76) * mm, "end": v(-5.61, -2.86) * mm});
            skLineSegment(sketch, "E329", {"start": v(-5.61, -2.86) * mm, "end": v(-5.56, -2.96) * mm});
            skLineSegment(sketch, "E330", {"start": v(-5.56, -2.96) * mm, "end": v(-5.41, -2.95) * mm});
            skLineSegment(sketch, "E331", {"start": v(-5.41, -2.95) * mm, "end": v(-5.27, -2.94) * mm});
            skLineSegment(sketch, "E332", {"start": v(-5.27, -2.94) * mm, "end": v(-5.13, -2.91) * mm});
            skLineSegment(sketch, "E333", {"start": v(-5.13, -2.91) * mm, "end": v(-5, -2.87) * mm});
            skLineSegment(sketch, "E334", {"start": v(-5, -2.87) * mm, "end": v(-4.87, -2.82) * mm});
            skLineSegment(sketch, "E335", {"start": v(-4.87, -2.82) * mm, "end": v(-4.8, -2.94) * mm});
            skLineSegment(sketch, "E336", {"start": v(-4.8, -2.94) * mm, "end": v(-4.72, -3.06) * mm});
            skLineSegment(sketch, "E337", {"start": v(-4.72, -3.06) * mm, "end": v(-4.83, -3.14) * mm});
            skLineSegment(sketch, "E338", {"start": v(-4.83, -3.14) * mm, "end": v(-4.92, -3.25) * mm});
            skLineSegment(sketch, "E339", {"start": v(-4.92, -3.25) * mm, "end": v(-5, -3.36) * mm});
            skLineSegment(sketch, "E340", {"start": v(-5, -3.36) * mm, "end": v(-5.09, -3.48) * mm});
            skLineSegment(sketch, "E341", {"start": v(-5.09, -3.48) * mm, "end": v(-5.16, -3.61) * mm});
            skLineSegment(sketch, "E342", {"start": v(-5.16, -3.61) * mm, "end": v(-5.1, -3.7) * mm});
            skLineSegment(sketch, "E343", {"start": v(-5.1, -3.7) * mm, "end": v(-5.03, -3.8) * mm});
            skLineSegment(sketch, "E344", {"start": v(-5.03, -3.8) * mm, "end": v(-4.88, -3.76) * mm});
            skLineSegment(sketch, "E345", {"start": v(-4.88, -3.76) * mm, "end": v(-4.74, -3.72) * mm});
            skLineSegment(sketch, "E346", {"start": v(-4.74, -3.72) * mm, "end": v(-4.6, -3.68) * mm});
            skLineSegment(sketch, "E347", {"start": v(-4.6, -3.68) * mm, "end": v(-4.48, -3.62) * mm});
            skLineSegment(sketch, "E348", {"start": v(-4.48, -3.62) * mm, "end": v(-4.37, -3.55) * mm});
            skLineSegment(sketch, "E349", {"start": v(-4.37, -3.55) * mm, "end": v(-4.28, -3.65) * mm});
            skLineSegment(sketch, "E350", {"start": v(-4.28, -3.65) * mm, "end": v(-4.19, -3.76) * mm});
            skLineSegment(sketch, "E351", {"start": v(-4.19, -3.76) * mm, "end": v(-4.28, -3.86) * mm});
            skLineSegment(sketch, "E352", {"start": v(-4.28, -3.86) * mm, "end": v(-4.35, -3.98) * mm});
            skLineSegment(sketch, "E353", {"start": v(-4.35, -3.98) * mm, "end": v(-4.42, -4.1) * mm});
            skLineSegment(sketch, "E354", {"start": v(-4.42, -4.1) * mm, "end": v(-4.48, -4.23) * mm});
            skLineSegment(sketch, "E355", {"start": v(-4.48, -4.23) * mm, "end": v(-4.53, -4.37) * mm});
            skLineSegment(sketch, "E356", {"start": v(-4.53, -4.37) * mm, "end": v(-4.45, -4.45) * mm});
            skLineSegment(sketch, "E357", {"start": v(-4.45, -4.45) * mm, "end": v(-4.37, -4.53) * mm});
            skLineSegment(sketch, "E358", {"start": v(-4.37, -4.53) * mm, "end": v(-4.23, -4.48) * mm});
            skLineSegment(sketch, "E359", {"start": v(-4.23, -4.48) * mm, "end": v(-4.1, -4.42) * mm});
            skLineSegment(sketch, "E360", {"start": v(-4.1, -4.42) * mm, "end": v(-3.98, -4.35) * mm});
            skLineSegment(sketch, "E361", {"start": v(-3.98, -4.35) * mm, "end": v(-3.86, -4.28) * mm});
            skLineSegment(sketch, "E362", {"start": v(-3.86, -4.28) * mm, "end": v(-3.76, -4.19) * mm});
            skLineSegment(sketch, "E363", {"start": v(-3.76, -4.19) * mm, "end": v(-3.65, -4.28) * mm});
            skLineSegment(sketch, "E364", {"start": v(-3.65, -4.28) * mm, "end": v(-3.55, -4.37) * mm});
            skLineSegment(sketch, "E365", {"start": v(-3.55, -4.37) * mm, "end": v(-3.62, -4.48) * mm});
            skLineSegment(sketch, "E366", {"start": v(-3.62, -4.48) * mm, "end": v(-3.68, -4.6) * mm});
            skLineSegment(sketch, "E367", {"start": v(-3.68, -4.6) * mm, "end": v(-3.72, -4.74) * mm});
            skLineSegment(sketch, "E368", {"start": v(-3.72, -4.74) * mm, "end": v(-3.76, -4.88) * mm});
            skLineSegment(sketch, "E369", {"start": v(-3.76, -4.88) * mm, "end": v(-3.8, -5.03) * mm});
            skLineSegment(sketch, "E370", {"start": v(-3.8, -5.03) * mm, "end": v(-3.7, -5.1) * mm});
            skLineSegment(sketch, "E371", {"start": v(-3.7, -5.1) * mm, "end": v(-3.61, -5.16) * mm});
            skLineSegment(sketch, "E372", {"start": v(-3.61, -5.16) * mm, "end": v(-3.48, -5.09) * mm});
            skLineSegment(sketch, "E373", {"start": v(-3.48, -5.09) * mm, "end": v(-3.36, -5) * mm});
            skLineSegment(sketch, "E374", {"start": v(-3.36, -5) * mm, "end": v(-3.25, -4.92) * mm});
            skLineSegment(sketch, "E375", {"start": v(-3.25, -4.92) * mm, "end": v(-3.14, -4.83) * mm});
            skLineSegment(sketch, "E376", {"start": v(-3.14, -4.83) * mm, "end": v(-3.06, -4.72) * mm});
            skLineSegment(sketch, "E377", {"start": v(-3.06, -4.72) * mm, "end": v(-2.94, -4.8) * mm});
            skLineSegment(sketch, "E378", {"start": v(-2.94, -4.8) * mm, "end": v(-2.82, -4.87) * mm});
            skLineSegment(sketch, "E379", {"start": v(-2.82, -4.87) * mm, "end": v(-2.87, -5) * mm});
            skLineSegment(sketch, "E380", {"start": v(-2.87, -5) * mm, "end": v(-2.91, -5.13) * mm});
            skLineSegment(sketch, "E381", {"start": v(-2.91, -5.13) * mm, "end": v(-2.94, -5.27) * mm});
            skLineSegment(sketch, "E382", {"start": v(-2.94, -5.27) * mm, "end": v(-2.95, -5.41) * mm});
            skLineSegment(sketch, "E383", {"start": v(-2.95, -5.41) * mm, "end": v(-2.96, -5.56) * mm});
            skLineSegment(sketch, "E384", {"start": v(-2.96, -5.56) * mm, "end": v(-2.86, -5.61) * mm});
            skLineSegment(sketch, "E385", {"start": v(-2.86, -5.61) * mm, "end": v(-2.76, -5.66) * mm});
            skLineSegment(sketch, "E386", {"start": v(-2.76, -5.66) * mm, "end": v(-2.64, -5.57) * mm});
            skLineSegment(sketch, "E387", {"start": v(-2.64, -5.57) * mm, "end": v(-2.53, -5.47) * mm});
            skLineSegment(sketch, "E388", {"start": v(-2.53, -5.47) * mm, "end": v(-2.44, -5.37) * mm});
            skLineSegment(sketch, "E389", {"start": v(-2.44, -5.37) * mm, "end": v(-2.35, -5.26) * mm});
            skLineSegment(sketch, "E390", {"start": v(-2.35, -5.26) * mm, "end": v(-2.28, -5.14) * mm});
            skLineSegment(sketch, "E391", {"start": v(-2.28, -5.14) * mm, "end": v(-2.15, -5.2) * mm});
            skLineSegment(sketch, "E392", {"start": v(-2.15, -5.2) * mm, "end": v(-2.03, -5.25) * mm});
            skLineSegment(sketch, "E393", {"start": v(-2.03, -5.25) * mm, "end": v(-2.06, -5.38) * mm});
            skLineSegment(sketch, "E394", {"start": v(-2.06, -5.38) * mm, "end": v(-2.07, -5.52) * mm});
            skLineSegment(sketch, "E395", {"start": v(-2.07, -5.52) * mm, "end": v(-2.08, -5.66) * mm});
            skLineSegment(sketch, "E396", {"start": v(-2.08, -5.66) * mm, "end": v(-2.07, -5.8) * mm});
            skLineSegment(sketch, "E397", {"start": v(-2.07, -5.8) * mm, "end": v(-2.05, -5.96) * mm});
            skLineSegment(sketch, "E398", {"start": v(-2.05, -5.96) * mm, "end": v(-1.95, -6) * mm});
            skLineSegment(sketch, "E399", {"start": v(-1.95, -6) * mm, "end": v(-1.84, -6.03) * mm});
            skLineSegment(sketch, "E400", {"start": v(-1.84, -6.03) * mm, "end": v(-1.74, -5.91) * mm});
            skLineSegment(sketch, "E401", {"start": v(-1.74, -5.91) * mm, "end": v(-1.65, -5.8) * mm});
            skLineSegment(sketch, "E402", {"start": v(-1.65, -5.8) * mm, "end": v(-1.57, -5.68) * mm});
            skLineSegment(sketch, "E403", {"start": v(-1.57, -5.68) * mm, "end": v(-1.5, -5.56) * mm});
            skLineSegment(sketch, "E404", {"start": v(-1.5, -5.56) * mm, "end": v(-1.45, -5.44) * mm});
            skLineSegment(sketch, "E405", {"start": v(-1.45, -5.44) * mm, "end": v(-1.31, -5.47) * mm});
            skLineSegment(sketch, "E406", {"start": v(-1.31, -5.47) * mm, "end": v(-1.18, -5.5) * mm});
            skLineSegment(sketch, "E407", {"start": v(-1.18, -5.5) * mm, "end": v(-1.2, -5.64) * mm});
            skLineSegment(sketch, "E408", {"start": v(-1.2, -5.64) * mm, "end": v(-1.18, -5.77) * mm});
            skLineSegment(sketch, "E409", {"start": v(-1.18, -5.77) * mm, "end": v(-1.17, -5.92) * mm});
            skLineSegment(sketch, "E410", {"start": v(-1.17, -5.92) * mm, "end": v(-1.14, -6.06) * mm});
            skLineSegment(sketch, "E411", {"start": v(-1.14, -6.06) * mm, "end": v(-1.1, -6.2) * mm});
            skLineSegment(sketch, "E412", {"start": v(-1.1, -6.2) * mm, "end": v(-0.99, -6.22) * mm});
            skLineSegment(sketch, "E413", {"start": v(-0.99, -6.22) * mm, "end": v(-0.87, -6.24) * mm});
            skLineSegment(sketch, "E414", {"start": v(-0.87, -6.24) * mm, "end": v(-0.8, -6.11) * mm});
            skLineSegment(sketch, "E415", {"start": v(-0.8, -6.11) * mm, "end": v(-0.72, -5.99) * mm});
            skLineSegment(sketch, "E416", {"start": v(-0.72, -5.99) * mm, "end": v(-0.66, -5.86) * mm});
            skLineSegment(sketch, "E417", {"start": v(-0.66, -5.86) * mm, "end": v(-0.6, -5.73) * mm});
            skLineSegment(sketch, "E418", {"start": v(-0.6, -5.73) * mm, "end": v(-0.58, -5.6) * mm});
            skLineSegment(sketch, "E419", {"start": v(-0.58, -5.6) * mm, "end": v(-0.44, -5.6) * mm});
            skLineSegment(sketch, "E420", {"start": v(-0.44, -5.6) * mm, "end": v(-0.3, -5.62) * mm});
            skLineSegment(sketch, "E421", {"start": v(-0.3, -5.62) * mm, "end": v(-0.3, -5.75) * mm});
            skLineSegment(sketch, "E422", {"start": v(-0.3, -5.75) * mm, "end": v(-0.27, -5.89) * mm});
            skLineSegment(sketch, "E423", {"start": v(-0.27, -5.89) * mm, "end": v(-0.23, -6.03) * mm});
            skLineSegment(sketch, "E424", {"start": v(-0.23, -6.03) * mm, "end": v(-0.17, -6.16) * mm});
            skLineSegment(sketch, "E425", {"start": v(-0.17, -6.16) * mm, "end": v(-0.11, -6.3) * mm});
            skLineSegment(sketch, "E426", {"start": v(-0.11, -6.3) * mm, "end": v(0, -6.3) * mm});
            skLineSegment(sketch, "E427", {"start": v(0, -6.3) * mm, "end": v(0.11, -6.3) * mm});
            skLineSegment(sketch, "E428", {"start": v(0.11, -6.3) * mm, "end": v(0.17, -6.16) * mm});
            skLineSegment(sketch, "E429", {"start": v(0.17, -6.16) * mm, "end": v(0.23, -6.03) * mm});
            skLineSegment(sketch, "E430", {"start": v(0.23, -6.03) * mm, "end": v(0.27, -5.89) * mm});
            skLineSegment(sketch, "E431", {"start": v(0.27, -5.89) * mm, "end": v(0.3, -5.75) * mm});
            skLineSegment(sketch, "E432", {"start": v(0.3, -5.75) * mm, "end": v(0.3, -5.62) * mm});
            skLineSegment(sketch, "E433", {"start": v(0.3, -5.62) * mm, "end": v(0.44, -5.6) * mm});
            skLineSegment(sketch, "E434", {"start": v(0.44, -5.6) * mm, "end": v(0.58, -5.6) * mm});
            skLineSegment(sketch, "E435", {"start": v(0.58, -5.6) * mm, "end": v(0.6, -5.73) * mm});
            skLineSegment(sketch, "E436", {"start": v(0.6, -5.73) * mm, "end": v(0.66, -5.86) * mm});
            skLineSegment(sketch, "E437", {"start": v(0.66, -5.86) * mm, "end": v(0.72, -5.99) * mm});
            skLineSegment(sketch, "E438", {"start": v(0.72, -5.99) * mm, "end": v(0.8, -6.11) * mm});
            skLineSegment(sketch, "E439", {"start": v(0.8, -6.11) * mm, "end": v(0.87, -6.24) * mm});
            skLineSegment(sketch, "E440", {"start": v(0.87, -6.24) * mm, "end": v(0.99, -6.22) * mm});
            skLineSegment(sketch, "E441", {"start": v(0.99, -6.22) * mm, "end": v(1.1, -6.2) * mm});
            skLineSegment(sketch, "E442", {"start": v(1.1, -6.2) * mm, "end": v(1.14, -6.06) * mm});
            skLineSegment(sketch, "E443", {"start": v(1.14, -6.06) * mm, "end": v(1.17, -5.92) * mm});
            skLineSegment(sketch, "E444", {"start": v(1.17, -5.92) * mm, "end": v(1.18, -5.77) * mm});
            skLineSegment(sketch, "E445", {"start": v(1.18, -5.77) * mm, "end": v(1.2, -5.64) * mm});
            skLineSegment(sketch, "E446", {"start": v(1.2, -5.64) * mm, "end": v(1.18, -5.5) * mm});
            skLineSegment(sketch, "E447", {"start": v(1.18, -5.5) * mm, "end": v(1.31, -5.47) * mm});
            skLineSegment(sketch, "E448", {"start": v(1.31, -5.47) * mm, "end": v(1.45, -5.44) * mm});
            skLineSegment(sketch, "E449", {"start": v(1.45, -5.44) * mm, "end": v(1.5, -5.56) * mm});
            skLineSegment(sketch, "E450", {"start": v(1.5, -5.56) * mm, "end": v(1.57, -5.68) * mm});
            skLineSegment(sketch, "E451", {"start": v(1.57, -5.68) * mm, "end": v(1.65, -5.8) * mm});
            skLineSegment(sketch, "E452", {"start": v(1.65, -5.8) * mm, "end": v(1.74, -5.91) * mm});
            skLineSegment(sketch, "E453", {"start": v(1.74, -5.91) * mm, "end": v(1.84, -6.03) * mm});
            skLineSegment(sketch, "E454", {"start": v(1.84, -6.03) * mm, "end": v(1.95, -6) * mm});
            skLineSegment(sketch, "E455", {"start": v(1.95, -6) * mm, "end": v(2.05, -5.96) * mm});
            skLineSegment(sketch, "E456", {"start": v(2.05, -5.96) * mm, "end": v(2.07, -5.8) * mm});
            skLineSegment(sketch, "E457", {"start": v(2.07, -5.8) * mm, "end": v(2.08, -5.66) * mm});
            skLineSegment(sketch, "E458", {"start": v(2.08, -5.66) * mm, "end": v(2.07, -5.52) * mm});
            skLineSegment(sketch, "E459", {"start": v(2.07, -5.52) * mm, "end": v(2.06, -5.38) * mm});
            skLineSegment(sketch, "E460", {"start": v(2.06, -5.38) * mm, "end": v(2.03, -5.25) * mm});
            skLineSegment(sketch, "E461", {"start": v(2.03, -5.25) * mm, "end": v(2.15, -5.2) * mm});
            skLineSegment(sketch, "E462", {"start": v(2.15, -5.2) * mm, "end": v(2.28, -5.14) * mm});
            skLineSegment(sketch, "E463", {"start": v(2.28, -5.14) * mm, "end": v(2.35, -5.26) * mm});
            skLineSegment(sketch, "E464", {"start": v(2.35, -5.26) * mm, "end": v(2.44, -5.37) * mm});
            skLineSegment(sketch, "E465", {"start": v(2.44, -5.37) * mm, "end": v(2.53, -5.47) * mm});
            skLineSegment(sketch, "E466", {"start": v(2.53, -5.47) * mm, "end": v(2.64, -5.57) * mm});
            skLineSegment(sketch, "E467", {"start": v(2.64, -5.57) * mm, "end": v(2.76, -5.66) * mm});
            skLineSegment(sketch, "E468", {"start": v(2.76, -5.66) * mm, "end": v(2.86, -5.61) * mm});
            skLineSegment(sketch, "E469", {"start": v(2.86, -5.61) * mm, "end": v(2.96, -5.56) * mm});
            skLineSegment(sketch, "E470", {"start": v(2.96, -5.56) * mm, "end": v(2.95, -5.41) * mm});
            skLineSegment(sketch, "E471", {"start": v(2.95, -5.41) * mm, "end": v(2.94, -5.27) * mm});
            skLineSegment(sketch, "E472", {"start": v(2.94, -5.27) * mm, "end": v(2.91, -5.13) * mm});
            skLineSegment(sketch, "E473", {"start": v(2.91, -5.13) * mm, "end": v(2.87, -5) * mm});
            skLineSegment(sketch, "E474", {"start": v(2.87, -5) * mm, "end": v(2.82, -4.87) * mm});
            skLineSegment(sketch, "E475", {"start": v(2.82, -4.87) * mm, "end": v(2.94, -4.8) * mm});
            skLineSegment(sketch, "E476", {"start": v(2.94, -4.8) * mm, "end": v(3.06, -4.72) * mm});
            skLineSegment(sketch, "E477", {"start": v(3.06, -4.72) * mm, "end": v(3.14, -4.83) * mm});
            skLineSegment(sketch, "E478", {"start": v(3.14, -4.83) * mm, "end": v(3.25, -4.92) * mm});
            skLineSegment(sketch, "E479", {"start": v(3.25, -4.92) * mm, "end": v(3.36, -5) * mm});
            skLineSegment(sketch, "E480", {"start": v(3.36, -5) * mm, "end": v(3.48, -5.09) * mm});
            skLineSegment(sketch, "E481", {"start": v(3.48, -5.09) * mm, "end": v(3.61, -5.16) * mm});
            skLineSegment(sketch, "E482", {"start": v(3.61, -5.16) * mm, "end": v(3.7, -5.1) * mm});
            skLineSegment(sketch, "E483", {"start": v(3.7, -5.1) * mm, "end": v(3.8, -5.03) * mm});
            skLineSegment(sketch, "E484", {"start": v(3.8, -5.03) * mm, "end": v(3.76, -4.88) * mm});
            skLineSegment(sketch, "E485", {"start": v(3.76, -4.88) * mm, "end": v(3.72, -4.74) * mm});
            skLineSegment(sketch, "E486", {"start": v(3.72, -4.74) * mm, "end": v(3.68, -4.6) * mm});
            skLineSegment(sketch, "E487", {"start": v(3.68, -4.6) * mm, "end": v(3.62, -4.48) * mm});
            skLineSegment(sketch, "E488", {"start": v(3.62, -4.48) * mm, "end": v(3.55, -4.37) * mm});
            skLineSegment(sketch, "E489", {"start": v(3.55, -4.37) * mm, "end": v(3.65, -4.28) * mm});
            skLineSegment(sketch, "E490", {"start": v(3.65, -4.28) * mm, "end": v(3.76, -4.19) * mm});
            skLineSegment(sketch, "E491", {"start": v(3.76, -4.19) * mm, "end": v(3.86, -4.28) * mm});
            skLineSegment(sketch, "E492", {"start": v(3.86, -4.28) * mm, "end": v(3.98, -4.35) * mm});
            skLineSegment(sketch, "E493", {"start": v(3.98, -4.35) * mm, "end": v(4.1, -4.42) * mm});
            skLineSegment(sketch, "E494", {"start": v(4.1, -4.42) * mm, "end": v(4.23, -4.48) * mm});
            skLineSegment(sketch, "E495", {"start": v(4.23, -4.48) * mm, "end": v(4.37, -4.53) * mm});
            skLineSegment(sketch, "E496", {"start": v(4.37, -4.53) * mm, "end": v(4.45, -4.45) * mm});
            skLineSegment(sketch, "E497", {"start": v(4.45, -4.45) * mm, "end": v(4.53, -4.37) * mm});
            skLineSegment(sketch, "E498", {"start": v(4.53, -4.37) * mm, "end": v(4.48, -4.23) * mm});
            skLineSegment(sketch, "E499", {"start": v(4.48, -4.23) * mm, "end": v(4.42, -4.1) * mm});
            skLineSegment(sketch, "E500", {"start": v(4.42, -4.1) * mm, "end": v(4.35, -3.98) * mm});
            skLineSegment(sketch, "E501", {"start": v(4.35, -3.98) * mm, "end": v(4.28, -3.86) * mm});
            skLineSegment(sketch, "E502", {"start": v(4.28, -3.86) * mm, "end": v(4.19, -3.76) * mm});
            skLineSegment(sketch, "E503", {"start": v(4.19, -3.76) * mm, "end": v(4.28, -3.65) * mm});
            skLineSegment(sketch, "E504", {"start": v(4.28, -3.65) * mm, "end": v(4.37, -3.55) * mm});
            skLineSegment(sketch, "E505", {"start": v(4.37, -3.55) * mm, "end": v(4.48, -3.62) * mm});
            skLineSegment(sketch, "E506", {"start": v(4.48, -3.62) * mm, "end": v(4.6, -3.68) * mm});
            skLineSegment(sketch, "E507", {"start": v(4.6, -3.68) * mm, "end": v(4.74, -3.72) * mm});
            skLineSegment(sketch, "E508", {"start": v(4.74, -3.72) * mm, "end": v(4.88, -3.76) * mm});
            skLineSegment(sketch, "E509", {"start": v(4.88, -3.76) * mm, "end": v(5.03, -3.8) * mm});
            skLineSegment(sketch, "E510", {"start": v(5.03, -3.8) * mm, "end": v(5.1, -3.7) * mm});
            skLineSegment(sketch, "E511", {"start": v(5.1, -3.7) * mm, "end": v(5.16, -3.61) * mm});
            skLineSegment(sketch, "E512", {"start": v(5.16, -3.61) * mm, "end": v(5.09, -3.48) * mm});
            skLineSegment(sketch, "E513", {"start": v(5.09, -3.48) * mm, "end": v(5, -3.36) * mm});
            skLineSegment(sketch, "E514", {"start": v(5, -3.36) * mm, "end": v(4.92, -3.25) * mm});
            skLineSegment(sketch, "E515", {"start": v(4.92, -3.25) * mm, "end": v(4.83, -3.14) * mm});
            skLineSegment(sketch, "E516", {"start": v(4.83, -3.14) * mm, "end": v(4.72, -3.06) * mm});
            skLineSegment(sketch, "E517", {"start": v(4.72, -3.06) * mm, "end": v(4.8, -2.94) * mm});
            skLineSegment(sketch, "E518", {"start": v(4.8, -2.94) * mm, "end": v(4.87, -2.82) * mm});
            skLineSegment(sketch, "E519", {"start": v(4.87, -2.82) * mm, "end": v(5, -2.87) * mm});
            skLineSegment(sketch, "E520", {"start": v(5, -2.87) * mm, "end": v(5.13, -2.91) * mm});
            skLineSegment(sketch, "E521", {"start": v(5.13, -2.91) * mm, "end": v(5.27, -2.94) * mm});
            skLineSegment(sketch, "E522", {"start": v(5.27, -2.94) * mm, "end": v(5.41, -2.95) * mm});
            skLineSegment(sketch, "E523", {"start": v(5.41, -2.95) * mm, "end": v(5.56, -2.96) * mm});
            skLineSegment(sketch, "E524", {"start": v(5.56, -2.96) * mm, "end": v(5.61, -2.86) * mm});
            skLineSegment(sketch, "E525", {"start": v(5.61, -2.86) * mm, "end": v(5.66, -2.76) * mm});
            skLineSegment(sketch, "E526", {"start": v(5.66, -2.76) * mm, "end": v(5.57, -2.64) * mm});
            skLineSegment(sketch, "E527", {"start": v(5.57, -2.64) * mm, "end": v(5.47, -2.53) * mm});
            skLineSegment(sketch, "E528", {"start": v(5.47, -2.53) * mm, "end": v(5.37, -2.44) * mm});
            skLineSegment(sketch, "E529", {"start": v(5.37, -2.44) * mm, "end": v(5.26, -2.35) * mm});
            skLineSegment(sketch, "E530", {"start": v(5.26, -2.35) * mm, "end": v(5.14, -2.28) * mm});
            skLineSegment(sketch, "E531", {"start": v(5.14, -2.28) * mm, "end": v(5.2, -2.15) * mm});
            skLineSegment(sketch, "E532", {"start": v(5.2, -2.15) * mm, "end": v(5.25, -2.03) * mm});
            skLineSegment(sketch, "E533", {"start": v(5.25, -2.03) * mm, "end": v(5.38, -2.06) * mm});
            skLineSegment(sketch, "E534", {"start": v(5.38, -2.06) * mm, "end": v(5.52, -2.07) * mm});
            skLineSegment(sketch, "E535", {"start": v(5.52, -2.07) * mm, "end": v(5.66, -2.08) * mm});
            skLineSegment(sketch, "E536", {"start": v(5.66, -2.08) * mm, "end": v(5.8, -2.07) * mm});
            skLineSegment(sketch, "E537", {"start": v(5.8, -2.07) * mm, "end": v(5.96, -2.05) * mm});
            skLineSegment(sketch, "E538", {"start": v(5.96, -2.05) * mm, "end": v(6, -1.95) * mm});
            skLineSegment(sketch, "E539", {"start": v(6, -1.95) * mm, "end": v(6.03, -1.84) * mm});
            skLineSegment(sketch, "E540", {"start": v(6.03, -1.84) * mm, "end": v(5.91, -1.74) * mm});
            skLineSegment(sketch, "E541", {"start": v(5.91, -1.74) * mm, "end": v(5.8, -1.65) * mm});
            skLineSegment(sketch, "E542", {"start": v(5.8, -1.65) * mm, "end": v(5.68, -1.57) * mm});
            skLineSegment(sketch, "E543", {"start": v(5.68, -1.57) * mm, "end": v(5.56, -1.5) * mm});
            skLineSegment(sketch, "E544", {"start": v(5.56, -1.5) * mm, "end": v(5.44, -1.45) * mm});
            skLineSegment(sketch, "E545", {"start": v(5.44, -1.45) * mm, "end": v(5.47, -1.31) * mm});
            skLineSegment(sketch, "E546", {"start": v(5.47, -1.31) * mm, "end": v(5.5, -1.18) * mm});
            skLineSegment(sketch, "E547", {"start": v(5.5, -1.18) * mm, "end": v(5.64, -1.2) * mm});
            skLineSegment(sketch, "E548", {"start": v(5.64, -1.2) * mm, "end": v(5.77, -1.18) * mm});
            skLineSegment(sketch, "E549", {"start": v(5.77, -1.18) * mm, "end": v(5.92, -1.17) * mm});
            skLineSegment(sketch, "E550", {"start": v(5.92, -1.17) * mm, "end": v(6.06, -1.14) * mm});
            skLineSegment(sketch, "E551", {"start": v(6.06, -1.14) * mm, "end": v(6.2, -1.1) * mm});
            skLineSegment(sketch, "E552", {"start": v(6.2, -1.1) * mm, "end": v(6.22, -0.99) * mm});
            skLineSegment(sketch, "E553", {"start": v(6.22, -0.99) * mm, "end": v(6.24, -0.87) * mm});
            skLineSegment(sketch, "E554", {"start": v(6.24, -0.87) * mm, "end": v(6.11, -0.8) * mm});
            skLineSegment(sketch, "E555", {"start": v(6.11, -0.8) * mm, "end": v(5.99, -0.72) * mm});
            skLineSegment(sketch, "E556", {"start": v(5.99, -0.72) * mm, "end": v(5.86, -0.66) * mm});
            skLineSegment(sketch, "E557", {"start": v(5.86, -0.66) * mm, "end": v(5.73, -0.6) * mm});
            skLineSegment(sketch, "E558", {"start": v(5.73, -0.6) * mm, "end": v(5.6, -0.58) * mm});
            skLineSegment(sketch, "E559", {"start": v(5.6, -0.44) * mm, "end": v(5.6, -0.58) * mm});
            skCircle(sketch, "E560", {"center": v(0, 0) * mm, "radius": 4.75 * mm});
            skSolve(sketch);
        }
        {
            var Q0;
            Q0 = qSketchRegion(id + "F0", true);
            extrude(context, id + "F1", {"entities" : qUnion([Q0]), "depth" : 1.5 * mm, "offsetDistance" : 25 * mm});
        }
        {
            var Q0;
            Q0=qCreatedBy(makeId("Top.planeOp"),FACE);
            var sketch = newSketch(context, id + "F2", { "sketchPlane" : qUnion([Q0])});
            skCircle(sketch, "E561", {"center": v(16.02, 0) * mm, "radius": 6 * mm});
            skCircle(sketch, "E562", {"center": v(16.02, 0) * mm, "radius": 4.75 * mm});
            skSolve(sketch);
        }
        {
            var Q0;
            Q0=makeQuery(id+"F2.imprint","IMPRINT",FACE,{"disambiguationData":[TD([[makeQuery(id+"F2.imprint","IMPRINT",EDGE,{"derivedFrom":sQuery(id+"F2.wireOp",EDGE,"E561")}),1.0]])]});
            extrude(context, id + "F3", {"entities" : qUnion([Q0]), "depth" : 1.5 * mm, "offsetDistance" : 25 * mm});
        }
    });
